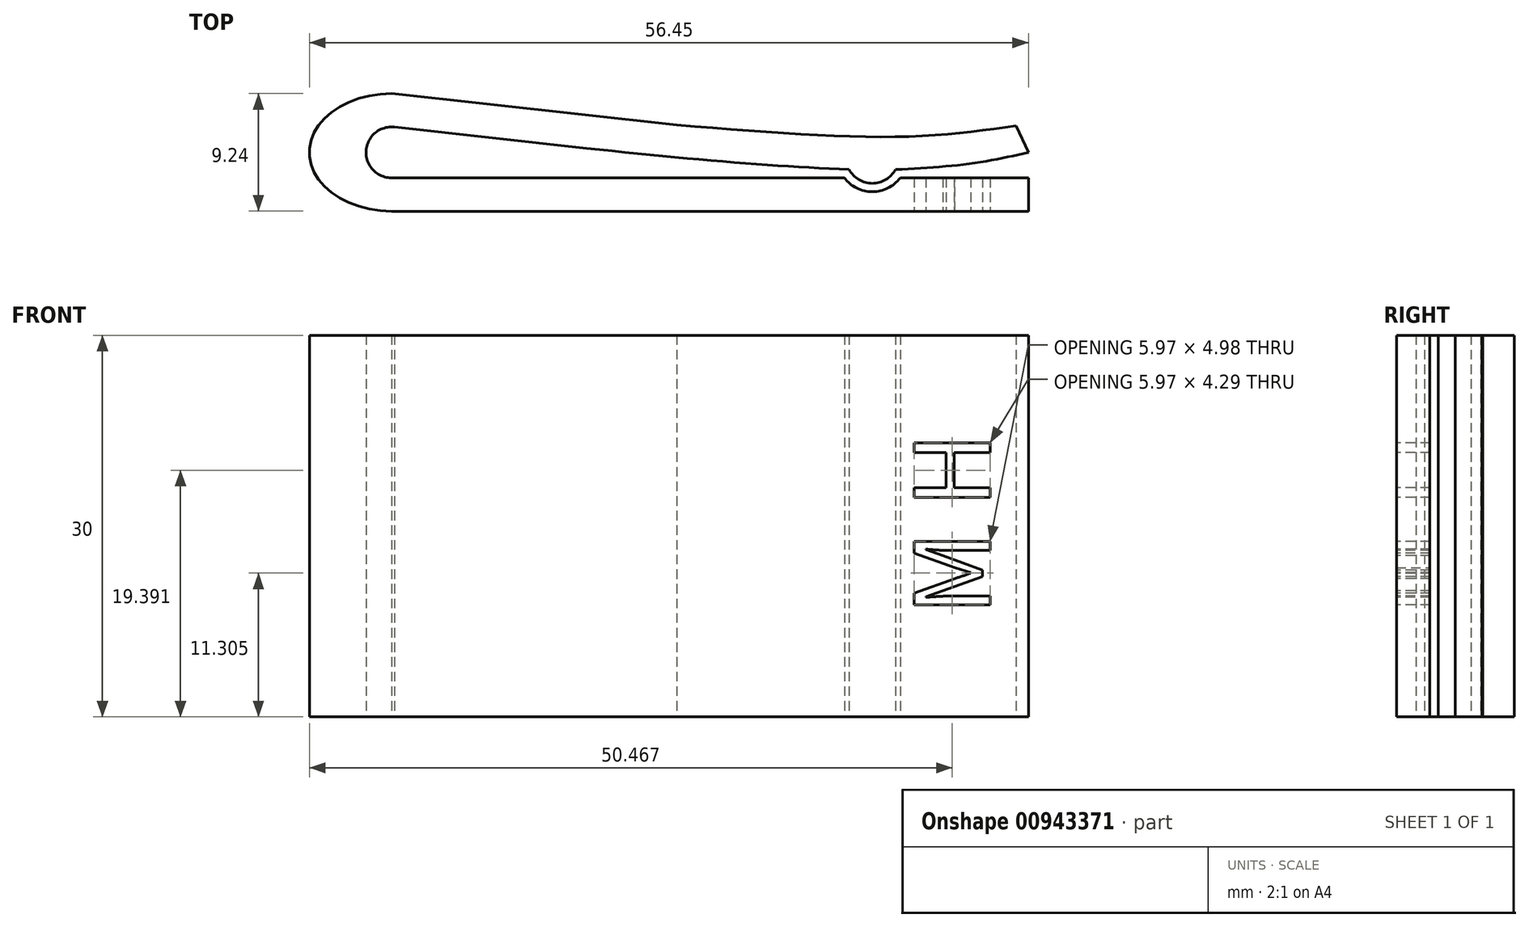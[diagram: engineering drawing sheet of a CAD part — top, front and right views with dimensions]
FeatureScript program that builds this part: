
annotation { "Feature Type Name" : "Feature", "Feature Type Description" : "" }
export const myFeature = defineFeature(function(context is Context, id is Id, definition is map)
    precondition{}
    {
        {
            var Q0;
            Q0=qCreatedBy(makeId("Top.planeOp"),FACE);
            var sketch = newSketch(context, id + "F0", { "sketchPlane" : qUnion([Q0])});
            skArc(sketch, "E0", {"start": v(0.24, 1.99) * mm, "mid": v(-2, 0.12) * mm, "end": v(0, -2) * mm});
            skLineSegment(sketch, "E1", {"start": v(0, -2) * mm, "end": v(33.22, -2) * mm});
            skLineSegment(sketch, "E2", {"start": v(15.31, 0.32) * mm, "end": v(0.2, 2) * mm});
            skPoint(sketch, "E3.end.orphan", {"position": v(0, 2.01) * mm});
            skLineSegment(sketch, "E4", {"start": v(22.4, 2.15) * mm, "end": v(0, 4.62) * mm});
            skLineSegment(sketch, "E5", {"start": v(0, -4.62) * mm, "end": v(50, -4.62) * mm});
            skEllipticalArc(sketch, "E6", {});
            skArc(sketch, "E7", {"start": v(35.55, -2) * mm, "mid": v(37.74, -3.1) * mm, "end": v(39.93, -2) * mm});
            skLineSegment(sketch, "E8", {"start": v(33.22, -2) * mm, "end": v(35.55, -2) * mm});
            skLineSegment(sketch, "E9", {"start": v(39.93, -2) * mm, "end": v(50, -2) * mm});
            skArc(sketch, "E10.trimOffspring", {"start": v(35.92, -1.35) * mm, "mid": v(37.74, -2.43) * mm, "end": v(39.57, -1.35) * mm});
            skLineSegment(sketch, "E11", {"start": v(50, 0) * mm, "end": v(49.03, 2.08) * mm});
            skFitSpline(sketch, "E12", {"points": [v(49.03, 2.08) * mm, v(39.93, 1.23) * mm, v(22.4, 2.15) * mm], "startDerivative": vector(-19.93, -2.8) * mm, "endDerivative": vector(-32.66, 2.64) * mm});
            skFitSpline(sketch, "E13", {"points": [v(50, 0) * mm, v(45.43, -0.88) * mm, v(39.57, -1.35) * mm], "startDerivative": vector(-9.39, -2.11) * mm, "endDerivative": vector(-11.44, -0.62) * mm});
            skPoint(sketch, "E14.orphan", {"position": v(50, -1.35) * mm});
            skPoint(sketch, "E15.orphan", {"position": v(50, 0.95) * mm});
            skFitSpline(sketch, "E16", {"points": [v(35.92, -1.35) * mm, v(27.3, -0.82) * mm, v(15.31, 0.32) * mm], "startDerivative": vector(-18.02, 0.94) * mm, "endDerivative": vector(-23.06, 2.36) * mm});
            skPoint(sketch, "E17.end.orphan", {"position": v(30.43, -1.35) * mm});
            skLineSegment(sketch, "E18", {"start": v(50, -2) * mm, "end": v(50, -4.62) * mm});
            const initialGuessF0  = {"E6": [0, 0, 0, 1, 0.004623365308887389, 0.0064499461705691385, 6.283185307179586, 3.141592653589793]};
            skSetInitialGuess(sketch, initialGuessF0);
            skSolve(sketch);
        }
        {
            var Q0;
            {var subQ6=sQuery(id+"F0.wireOp",EDGE,"E1");Q0=makeQuery(id+"F0.imprint","IMPRINT",FACE,{"disambiguationData":[TD([[makeQuery(id+"F0.imprint","IMPRINT",EDGE,{"derivedFrom":subQ6}),-1.0]])]});}
            extrude(context, id + "F1", {"entities" : qUnion([Q0]), "depth" : 30 * mm});
        }
        {
            var Q0;
            Q0=makeQuery(id+"F1.opExtrude","SWEPT_FACE",FACE,{"disambiguationData":[OSD([sQuery(id+"F0.wireOp",EDGE,"E5")])]});
            var sketch = newSketch(context, id + "F2", { "sketchPlane" : qUnion([Q0])});
            skLineSegment(sketch, "E19", {"start": v(24.3, 24.9) * mm, "end": v(5.22, 18.7) * mm});
            skLineSegment(sketch, "E20", {"start": v(5.22, 18.7) * mm, "end": v(31.27, 10.06) * mm});
            skLineSegment(sketch, "E21", {"start": v(24.3, 24.9) * mm, "end": v(31.27, 10.06) * mm});
            skLineSegment(sketch, "E22", {"start": v(31.27, 10.06) * mm, "end": v(33.47, 5.37) * mm});
            skLineSegment(sketch, "E23", {"start": v(33.47, 5.37) * mm, "end": v(39.22, 3.5) * mm});
            skLineSegment(sketch, "E24", {"start": v(39.22, 24.31) * mm, "end": v(26.52, 20.18) * mm});
            skLineSegment(sketch, "E25", {"start": v(26.52, 20.18) * mm, "end": v(13.52, 15.95) * mm});
            skLineSegment(sketch, "E26", {"start": v(26.52, 20.18) * mm, "end": v(33.47, 5.37) * mm});
            skLineSegment(sketch, "E27", {"start": v(39.22, 24.31) * mm, "end": v(39.22, 3.5) * mm});
            skSolve(sketch);
        }
        {
            var Q0;
            {var subQ5=sQuery(id+"F2.wireOp",EDGE,"E19");Q0=makeQuery(id+"F2.imprint","IMPRINT",FACE,{"disambiguationData":[TD([[makeQuery(id+"F2.imprint","IMPRINT",EDGE,{"derivedFrom":subQ5}),-1.0]])]});}
            var sketch = newSketch(context, id + "F3", { "sketchPlane" : qUnion([Q0])});
            skText(sketch, "E28", { "text": "M H", "fontName": "NotoSansCJKsc-Regular.otf"});
            const initialGuessF3  = {"E28": [0.047, 0.008, 0, 1, 0.00586]};
            skSetInitialGuess(sketch, initialGuessF3);
            skSolve(sketch);
        }
        {
            var Q0;
            Q0 = qSketchRegion(id + "F3", true);
            extrude(context, id + "F4", {"entities" : qUnion([Q0]), "operationType" : NewBodyOperationType.REMOVE, "endBound" : BoundingType.UP_TO_NEXT, "oppositeDirection" : true, "depth" : 25 * mm, "offsetDistance" : 25 * mm});
        }
    });
